# Revit family: xBath-Shower-American_Standard-Studio_S-T105.50X_Series
name_source: partatom
category: Plumbing Fixtures
revit_build: Autodesk Revit 2014 (Build: 20130308_1515(x64)
units: mm (PartAtom-declared; Revit-internal decimal feet)

## types (3) — shared parameters
ADA Compliant = Yes
Assembly Code = D2020300
CW Connection = Yes
CWFU = 3
Default Elevation = 40"
Finish = Metal-American Standard-002-Polished Chrome
Flow Rate = 2.5 gpm/ 9.5 L/min. flow rate.
HW Connection = Yes
HWFU = 3
Height = 4 1/2"
Installation Type = Wall Mounted
Length = 11 7/8"
Manufacturer = American Standard
Material = Metal-American Standard-002-Polished Chrome
Price = Prices may vary. Please consult Manufacturer Representative for most up-to-date price list.
Product Documentation Link = https://www.americanstandard-us.com
Product Page URL = https://www.americanstandard-us.com
Spacing from Wall = 2"
Specification = Bath/shower filling shall feature modern rain showerhead with Max. 2.5 gpm/ 9.5 L/min. flow rate
Third Connection = 1/2"
URL = https://www.americanstandard-us.com
Valve = Yes
Vent Connection = No
WFU = 4
Warranty Information = One Year Limited Warranty
Waste Connection = Yes
Water Connection Diameter = 1/2"
Water Connection Radius = 1/4"
Width = 7 1/2"

## per-type parameters (varying)
| type | Bath | Description | Shower |
| T105.502 | Yes | Studio S Pressure Balance Bath/Shower Trim Kit. Metal Lever Handle. LESS Valve Body. | Yes |
| T105.501 | No | Studio S Pressure Balance Shower Trim Kit. Metal Lever Handle. LESS Valve Body. | Yes |
| T105.500 | No | Studio S Pressure Balance Valve Only Trim Kit. Metal Lever Handle. LESS Valve Body. | No |

note: column(s) folded — value = type name in every type: Model

## geometry (parser evidence)
native form markers: Sweep x2
no freeform markers — native parametric forms only
